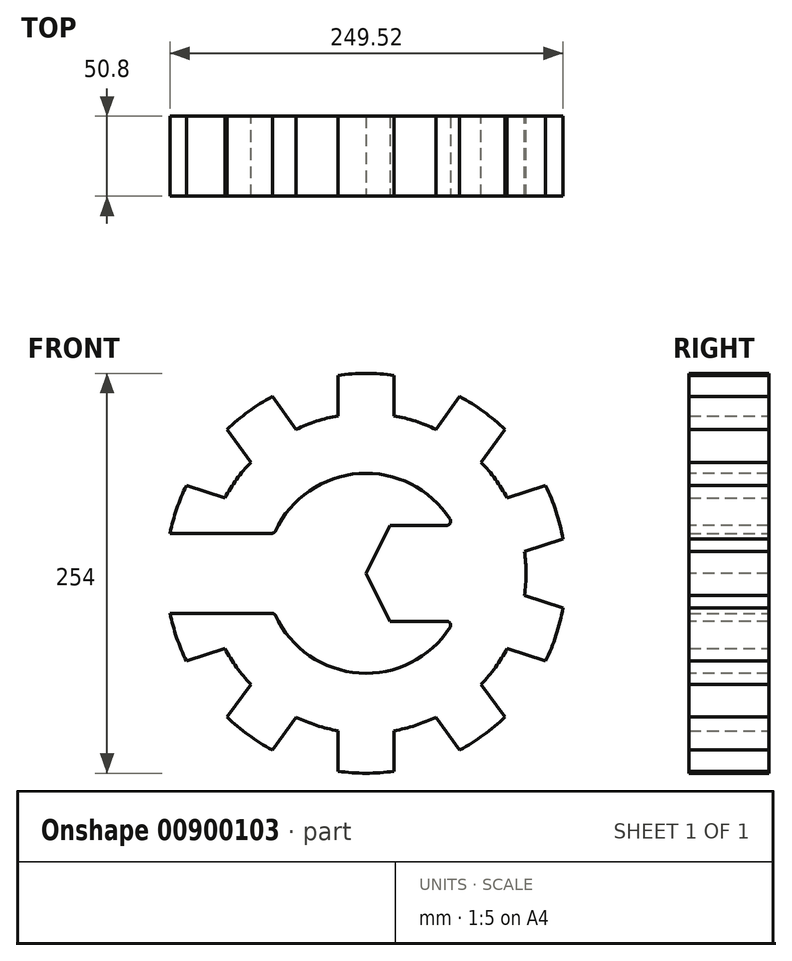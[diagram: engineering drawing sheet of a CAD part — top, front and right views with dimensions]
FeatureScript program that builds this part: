
annotation { "Feature Type Name" : "Feature", "Feature Type Description" : "" }
export const myFeature = defineFeature(function(context is Context, id is Id, definition is map)
    precondition{}
    {
        {
            var Q0;
            Q0=qCreatedBy(makeId("Front.planeOp"),FACE);
            var sketch = newSketch(context, id + "F0", { "sketchPlane" : qUnion([Q0])});
            skArc(sketch, "E0", {"start": v(17.78, 125.75) * mm, "mid": v(0, 127) * mm, "end": v(-17.78, 125.75) * mm});
            skCircle(sketch, "E1", {"center": v(0, 0) * mm, "radius": 101.6 * mm});
            skLineSegment(sketch, "E2", {"start": v(0, 0) * mm, "end": v(0, 161.5) * mm, "construction": true});
            skLineSegment(sketch, "E3", {"start": v(17.78, 125.75) * mm, "end": v(17.78, 100.03) * mm});
            skLineSegment(sketch, "E4", {"start": v(-17.78, 125.75) * mm, "end": v(-17.78, 100.03) * mm});
            skArc(sketch, "E5.1.0", {"start": v(-59.53, 112.18) * mm, "mid": v(-74.65, 102.75) * mm, "end": v(-88.3, 91.28) * mm});
            skLineSegment(sketch, "E5.1.1", {"start": v(-59.53, 112.18) * mm, "end": v(-44.41, 91.38) * mm});
            skLineSegment(sketch, "E5.1.2", {"start": v(-88.3, 91.28) * mm, "end": v(-73.18, 70.48) * mm});
            skArc(sketch, "E5.2.0", {"start": v(-114.1, 55.77) * mm, "mid": v(-120.78, 39.25) * mm, "end": v(-125.09, 21.95) * mm});
            skLineSegment(sketch, "E5.2.1", {"start": v(-114.1, 55.77) * mm, "end": v(-89.64, 47.82) * mm});
            skLineSegment(sketch, "E5.2.2", {"start": v(-125.09, 21.95) * mm, "end": v(-100.63, 14) * mm});
            skArc(sketch, "E5.3.0", {"start": v(-125.09, -21.95) * mm, "mid": v(-120.78, -39.25) * mm, "end": v(-114.1, -55.77) * mm});
            skLineSegment(sketch, "E5.3.1", {"start": v(-125.09, -21.95) * mm, "end": v(-100.63, -14) * mm});
            skLineSegment(sketch, "E5.3.2", {"start": v(-114.1, -55.77) * mm, "end": v(-89.64, -47.82) * mm});
            skArc(sketch, "E5.4.0", {"start": v(-88.3, -91.28) * mm, "mid": v(-74.65, -102.75) * mm, "end": v(-59.53, -112.18) * mm});
            skLineSegment(sketch, "E5.4.1", {"start": v(-88.3, -91.28) * mm, "end": v(-73.18, -70.48) * mm});
            skLineSegment(sketch, "E5.4.2", {"start": v(-59.53, -112.18) * mm, "end": v(-44.41, -91.38) * mm});
            skArc(sketch, "E5.5.0", {"start": v(-17.78, -125.75) * mm, "mid": v(0, -127) * mm, "end": v(17.78, -125.75) * mm});
            skLineSegment(sketch, "E5.5.1", {"start": v(-17.78, -125.75) * mm, "end": v(-17.78, -100.03) * mm});
            skLineSegment(sketch, "E5.5.2", {"start": v(17.78, -125.75) * mm, "end": v(17.78, -100.03) * mm});
            skArc(sketch, "E6.3.6.0", {"start": v(59.53, -112.18) * mm, "mid": v(74.65, -102.75) * mm, "end": v(88.3, -91.28) * mm});
            skLineSegment(sketch, "E6.4.6.0", {"start": v(59.53, -112.18) * mm, "end": v(44.41, -91.38) * mm});
            skLineSegment(sketch, "E6.7.6.0", {"start": v(88.3, -91.28) * mm, "end": v(73.18, -70.48) * mm});
            skArc(sketch, "E7.3.7.0", {"start": v(114.1, -55.77) * mm, "mid": v(120.78, -39.25) * mm, "end": v(125.09, -21.95) * mm});
            skLineSegment(sketch, "E7.4.7.0", {"start": v(114.1, -55.77) * mm, "end": v(89.64, -47.82) * mm});
            skLineSegment(sketch, "E7.7.7.0", {"start": v(125.09, -21.95) * mm, "end": v(100.63, -14) * mm});
            skArc(sketch, "E8.3.8.0", {"start": v(125.09, 21.95) * mm, "mid": v(120.78, 39.25) * mm, "end": v(114.1, 55.77) * mm});
            skLineSegment(sketch, "E8.4.8.0", {"start": v(125.09, 21.95) * mm, "end": v(100.63, 14) * mm});
            skLineSegment(sketch, "E8.7.8.0", {"start": v(114.1, 55.77) * mm, "end": v(89.64, 47.82) * mm});
            skArc(sketch, "E8.3.9.0", {"start": v(88.3, 91.28) * mm, "mid": v(74.65, 102.75) * mm, "end": v(59.53, 112.18) * mm});
            skLineSegment(sketch, "E8.4.9.0", {"start": v(88.3, 91.28) * mm, "end": v(73.18, 70.48) * mm});
            skLineSegment(sketch, "E8.7.9.0", {"start": v(59.53, 112.18) * mm, "end": v(44.41, 91.38) * mm});
            skSolve(sketch);
        }
        {
            var Q0;
            Q0 = qSketchRegion(id + "F0", true);
            extrude(context, id + "F1", {"entities" : qUnion([Q0]), "depth" : 50.8 * mm, "offsetDistance" : 25.4 * mm});
        }
        {
            var Q0;
            Q0=makeQuery(id+"F1.opExtrude","CAP_FACE",FACE,{"disambiguationData":[OSD([sQuery(id+"F0.wireOp",EDGE,"E0"),sQuery(id+"F0.wireOp",EDGE,"E1"),sQuery(id+"F0.wireOp",EDGE,"E3"),sQuery(id+"F0.wireOp",EDGE,"E4"),sQuery(id+"F0.wireOp",EDGE,"E5.1.0"),sQuery(id+"F0.wireOp",EDGE,"E5.1.1"),sQuery(id+"F0.wireOp",EDGE,"E5.1.2"),sQuery(id+"F0.wireOp",EDGE,"E5.2.0"),sQuery(id+"F0.wireOp",EDGE,"E5.2.1"),sQuery(id+"F0.wireOp",EDGE,"E5.2.2"),sQuery(id+"F0.wireOp",EDGE,"E5.3.0"),sQuery(id+"F0.wireOp",EDGE,"E5.3.1"),sQuery(id+"F0.wireOp",EDGE,"E5.3.2"),sQuery(id+"F0.wireOp",EDGE,"E5.4.0"),sQuery(id+"F0.wireOp",EDGE,"E5.4.1"),sQuery(id+"F0.wireOp",EDGE,"E5.4.2"),sQuery(id+"F0.wireOp",EDGE,"E5.5.0"),sQuery(id+"F0.wireOp",EDGE,"E5.5.1"),sQuery(id+"F0.wireOp",EDGE,"E5.5.2"),sQuery(id+"F0.wireOp",EDGE,"E6.3.6.0"),sQuery(id+"F0.wireOp",EDGE,"E6.4.6.0"),sQuery(id+"F0.wireOp",EDGE,"E6.7.6.0")])],"isStart":false});
            var sketch = newSketch(context, id + "F2", { "sketchPlane" : qUnion([Q0])});
            skArc(sketch, "E9", {"start": v(53.38, 34.4) * mm, "mid": v(-4.3, 63.35) * mm, "end": v(-57.54, 26.87) * mm});
            skLineSegment(sketch, "E10", {"start": v(0, 0) * mm, "end": v(-80.5, 0) * mm, "construction": true});
            skLineSegment(sketch, "E11", {"start": v(-59.84, 25.4) * mm, "end": v(-136.04, 25.4) * mm});
            skLineSegment(sketch, "E12", {"start": v(-59.84, -25.4) * mm, "end": v(-136.04, -25.4) * mm});
            skLineSegment(sketch, "E13", {"start": v(51.24, 30.48) * mm, "end": v(15.24, 30.48) * mm});
            skLineSegment(sketch, "E14", {"start": v(15.24, 30.48) * mm, "end": v(0, 0) * mm});
            skLineSegment(sketch, "E15", {"start": v(0, 0) * mm, "end": v(15.24, -30.48) * mm});
            skLineSegment(sketch, "E16", {"start": v(15.24, -30.48) * mm, "end": v(51.24, -30.48) * mm});
            skLineSegment(sketch, "E17", {"start": v(-136.04, -25.4) * mm, "end": v(-136.04, 25.4) * mm});
            skArc(sketch, "E18.trimOffspring", {"start": v(-57.54, -26.87) * mm, "mid": v(-4.3, -63.35) * mm, "end": v(53.38, -34.4) * mm});
            skPoint(sketch, "E19.visualSharp", {"position": v(55.7, 30.48) * mm});
            skArc(sketch, "E19.filletArc", {"start": v(51.24, 30.48) * mm, "mid": v(53.47, 31.8) * mm, "end": v(53.38, 34.4) * mm});
            skPoint(sketch, "E20.visualSharp", {"position": v(55.7, -30.48) * mm});
            skArc(sketch, "E20.filletArc", {"start": v(53.38, -34.4) * mm, "mid": v(53.47, -31.8) * mm, "end": v(51.24, -30.48) * mm});
            skPoint(sketch, "E21.visualSharp", {"position": v(-58.2, 25.4) * mm});
            skArc(sketch, "E21.filletArc", {"start": v(-59.84, 25.4) * mm, "mid": v(-58.47, 25.8) * mm, "end": v(-57.54, 26.87) * mm});
            skPoint(sketch, "E22.visualSharp", {"position": v(-58.2, -25.4) * mm});
            skArc(sketch, "E22.filletArc", {"start": v(-57.54, -26.87) * mm, "mid": v(-58.47, -25.8) * mm, "end": v(-59.84, -25.4) * mm});
            skSolve(sketch);
        }
        {
            var Q0;
            Q0 = qSketchRegion(id + "F2", true);
            extrude(context, id + "F3", {"entities" : qUnion([Q0]), "operationType" : NewBodyOperationType.REMOVE, "oppositeDirection" : true, "depth" : 50.8 * mm, "offsetDistance" : 25.4 * mm});
        }
    });
